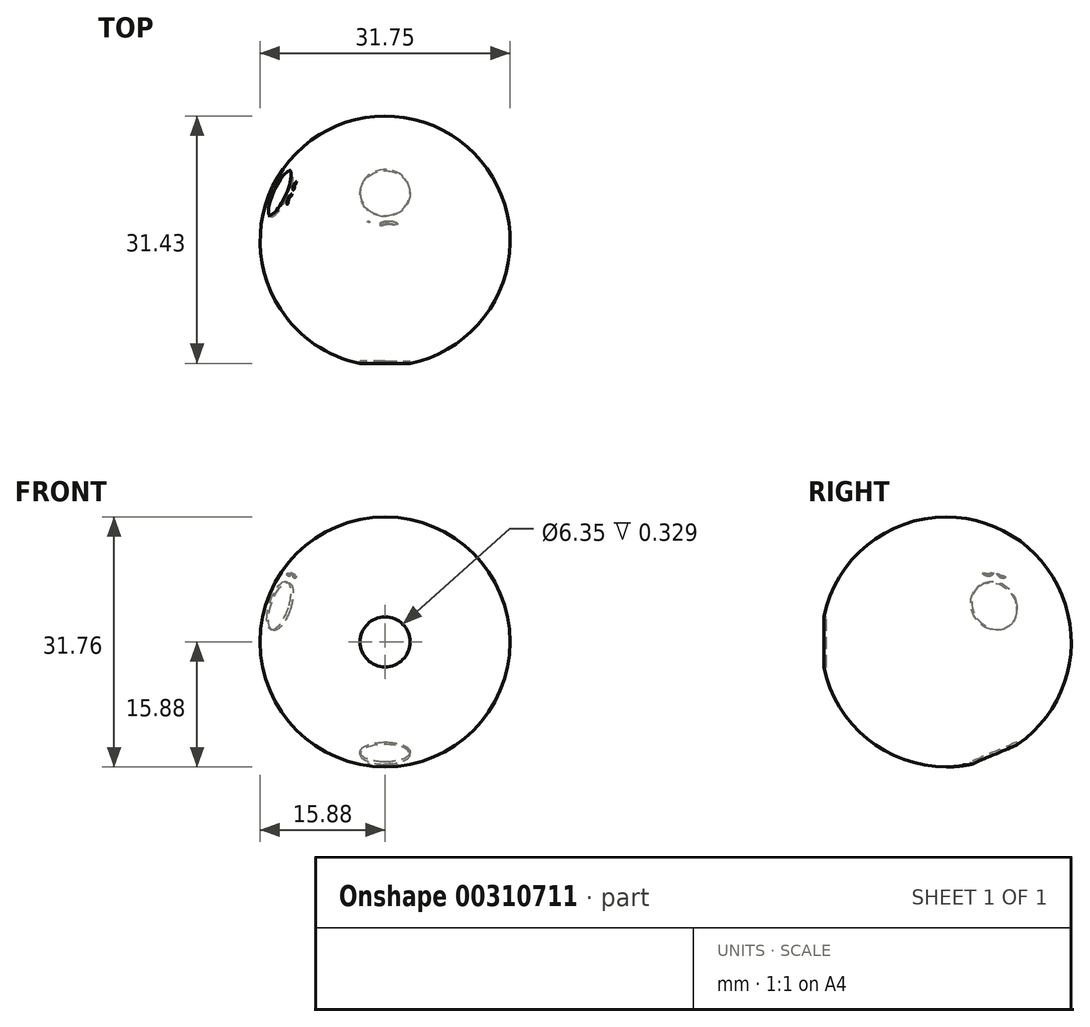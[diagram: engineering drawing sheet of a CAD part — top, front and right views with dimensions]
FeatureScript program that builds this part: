
annotation { "Feature Type Name" : "Feature", "Feature Type Description" : "" }
export const myFeature = defineFeature(function(context is Context, id is Id, definition is map)
    precondition{}
    {
        {
            var Q0;
            Q0=qCreatedBy(makeId("Front.planeOp"),FACE);
            var sketch = newSketch(context, id + "F0", { "sketchPlane" : qUnion([Q0])});
            skArc(sketch, "E0", {"start": v(0, 15.88) * mm, "mid": v(-15.88, 0) * mm, "end": v(0, -15.88) * mm});
            skLineSegment(sketch, "E1", {"start": v(0, 15.88) * mm, "end": v(0, -15.88) * mm});
            skSolve(sketch);
        }
        {
            var Q0;
            Q0=qCreatedBy(makeId("Top.planeOp"),FACE);
            var sketch = newSketch(context, id + "F1", { "sketchPlane" : qUnion([Q0])});
            skCircle(sketch, "E2", {"center": v(0, 0) * mm, "radius": 15.88 * mm});
            skSolve(sketch);
        }
        {
            var Q0;
            Q0=makeQuery(id+"F0.imprint","IMPRINT",FACE,{"disambiguationData":[TD([[makeQuery(id+"F0.imprint","IMPRINT",EDGE,{"derivedFrom":sQuery(id+"F0.wireOp",EDGE,"E0")}),1.0]])]});
            var Q1;
            Q1=sQuery(id+"F1.wireOp",EDGE,"E2");
            revolve(context, id + "F2", {"entities" : qUnion([Q0]), "axis" : qUnion([Q1]), "revolveType" : RevolveType.FULL});
        }
        {
            var Q0;
            Q0=qCreatedBy(makeId("Front.planeOp"),FACE);
            cPlane(context, id + "F3", {"entities" : qUnion([Q0]), "cplaneType" : CPlaneType.OFFSET, "offset" : 15.24 * mm, "width" : 152.4 * mm, "height" : 152.4 * mm});
        }
        {
            var Q0;
            Q0=qCreatedBy(id+"F3.planeOp",FACE);
            cPlane(context, id + "F4", {"entities" : qUnion([Q0]), "cplaneType" : CPlaneType.OFFSET, "offset" : 3 / 203.2 * mm, "oppositeDirection" : true, "width" : 152.4 * mm, "height" : 152.4 * mm});
        }
        {
            var Q0;
            Q0=qCreatedBy(id+"F4.planeOp",FACE);
            var sketch = newSketch(context, id + "F5", { "sketchPlane" : qUnion([Q0])});
            skCircle(sketch, "E3", {"center": v(0, 0) * mm, "radius": 3.18 * mm});
            skSolve(sketch);
        }
        {
            var Q0;
            Q0 = qSketchRegion(id + "F5", true);
            extrude(context, id + "F6", {"entities" : qUnion([Q0]), "depth" : 50.8 * mm});
        }
        {
            var Q0;
            Q0=qCreatedBy(makeId("Front.planeOp"),FACE);
            var sketch = newSketch(context, id + "F7", { "sketchPlane" : qUnion([Q0])});
            skLineSegment(sketch, "E4", {"start": v(0, 0) * mm, "end": v(67.72, 0) * mm, "construction": true});
            skLineSegment(sketch, "E5", {"start": v(0, 0) * mm, "end": v(-61.66, 0) * mm, "construction": true});
            skSolve(sketch);
        }
        {
            var Q0;
            Q0=qCreatedBy(makeId("Top.planeOp"),FACE);
            var sketch = newSketch(context, id + "F8", { "sketchPlane" : qUnion([Q0])});
            skLineSegment(sketch, "E6", {"start": v(0, 0) * mm, "end": v(0, 64.5) * mm, "construction": true});
            skSolve(sketch);
        }
        {
            var Q0;
            Q0=makeQuery(id+"F6.opExtrude","SWEPT_BODY",BODY,{"disambiguationData":[OSD([sQuery(id+"F5.wireOp",EDGE,"E3")])]});
            var Q1;
            Q1=sQuery(id+"F7.wireOp",EDGE,"E4");
            transform(context, id + "F9", {"entities" : qUnion([Q0]), "transformType" : TransformType.ROTATION, "transformAxis" : qUnion([Q1]), "angle" : 113.3 * degree, "makeCopy" : true});
        }
        {
            var Q0;
            Q0=makeQuery(id+"F9.opPattern","COPY",FACE,{"derivedFrom":makeQuery(id+"F6.opExtrude","CAP_FACE",FACE,{"disambiguationData":[OSD([sQuery(id+"F5.wireOp",EDGE,"E3")])],"isStart":false}),"instanceName":"1"});
            cPlane(context, id + "F10", {"entities" : qUnion([Q0]), "cplaneType" : CPlaneType.OFFSET, "offset" : 25.4 * mm, "oppositeDirection" : true, "width" : 152.4 * mm, "height" : 152.4 * mm});
        }
        {
            var Q0;
            Q0=qCreatedBy(id+"F10.planeOp",FACE);
            var sketch = newSketch(context, id + "F11", { "sketchPlane" : qUnion([Q0])});
            skText(sketch, "E7", { "text": "113.3", "fontName": "OpenSans-Regular.ttf"});
            const initialGuessF11  = {"E7": [-0.00688, 0.0039, 1, 0, 0.00383]};
            skSetInitialGuess(sketch, initialGuessF11);
            skSolve(sketch);
        }
        {
            var Q0;
            Q0 = qSketchRegion(id + "F11", true);
            extrude(context, id + "F12", {"entities" : qUnion([Q0]), "operationType" : NewBodyOperationType.REMOVE, "oppositeDirection" : true, "depth" : 25.4 * mm});
        }
        {
            var Q0;
            Q0=makeQuery(id+"F9.opPattern","COPY",BODY,{"derivedFrom":makeQuery(id+"F6.opExtrude","SWEPT_BODY",BODY,{"disambiguationData":[OSD([sQuery(id+"F5.wireOp",EDGE,"E3")])]}),"instanceName":"1"});
            var Q1;
            Q1=sQuery(id+"F8.wireOp",EDGE,"E6");
            transform(context, id + "F13", {"entities" : qUnion([Q0]), "transformType" : TransformType.ROTATION, "transformAxis" : qUnion([Q1]), "angle" : 108.8 * degree, "makeCopy" : true});
        }
        {
            var Q0;
            Q0=makeQuery(id+"F13.opPattern","COPY",FACE,{"derivedFrom":makeQuery(id+"F9.opPattern","COPY",FACE,{"derivedFrom":makeQuery(id+"F6.opExtrude","CAP_FACE",FACE,{"disambiguationData":[OSD([sQuery(id+"F5.wireOp",EDGE,"E3")])],"isStart":false}),"instanceName":"1"}),"instanceName":"1"});
            cPlane(context, id + "F14", {"entities" : qUnion([Q0]), "cplaneType" : CPlaneType.OFFSET, "offset" : 25.4 * mm, "oppositeDirection" : true, "width" : 152.4 * mm, "height" : 152.4 * mm});
        }
        {
            var Q0;
            Q0=qCreatedBy(id+"F14.planeOp",FACE);
            var sketch = newSketch(context, id + "F15", { "sketchPlane" : qUnion([Q0])});
            skText(sketch, "E8", { "text": "108.8", "fontName": "OpenSans-Regular.ttf"});
            const initialGuessF15  = {"E8": [-0.0042, 0.00403, 1, 0, 0.00255]};
            skSetInitialGuess(sketch, initialGuessF15);
            skSolve(sketch);
        }
        {
            var Q0;
            Q0 = qSketchRegion(id + "F15", true);
            extrude(context, id + "F16", {"entities" : qUnion([Q0]), "operationType" : NewBodyOperationType.REMOVE, "oppositeDirection" : true, "depth" : 25.4 * mm});
        }
        {
            var Q0;
            Q0=makeQuery(id+"F6.opExtrude","SWEPT_BODY",BODY,{"disambiguationData":[OSD([sQuery(id+"F5.wireOp",EDGE,"E3")])]});
            var Q1;
            Q1=makeQuery(id+"F13.opPattern","COPY",BODY,{"derivedFrom":makeQuery(id+"F9.opPattern","COPY",BODY,{"derivedFrom":makeQuery(id+"F6.opExtrude","SWEPT_BODY",BODY,{"disambiguationData":[OSD([sQuery(id+"F5.wireOp",EDGE,"E3")])]}),"instanceName":"1"}),"instanceName":"1"});
            var Q2;
            Q2=makeQuery(id+"F9.opPattern","COPY",BODY,{"derivedFrom":makeQuery(id+"F6.opExtrude","SWEPT_BODY",BODY,{"disambiguationData":[OSD([sQuery(id+"F5.wireOp",EDGE,"E3")])]}),"instanceName":"1"});
            var Q3;
            Q3=makeQuery(id+"F2.opRevolve","SWEPT_BODY",BODY,{"disambiguationData":[OSD([sQuery(id+"F0.wireOp",EDGE,"E0"),sQuery(id+"F0.wireOp",EDGE,"E1")])]});
            booleanBodies(context, id + "F17", {"operationType" : BooleanOperationType.SUBTRACTION, "tools" : qUnion([Q0, Q1, Q2]), "targets" : qUnion([Q3])});
        }
    });
